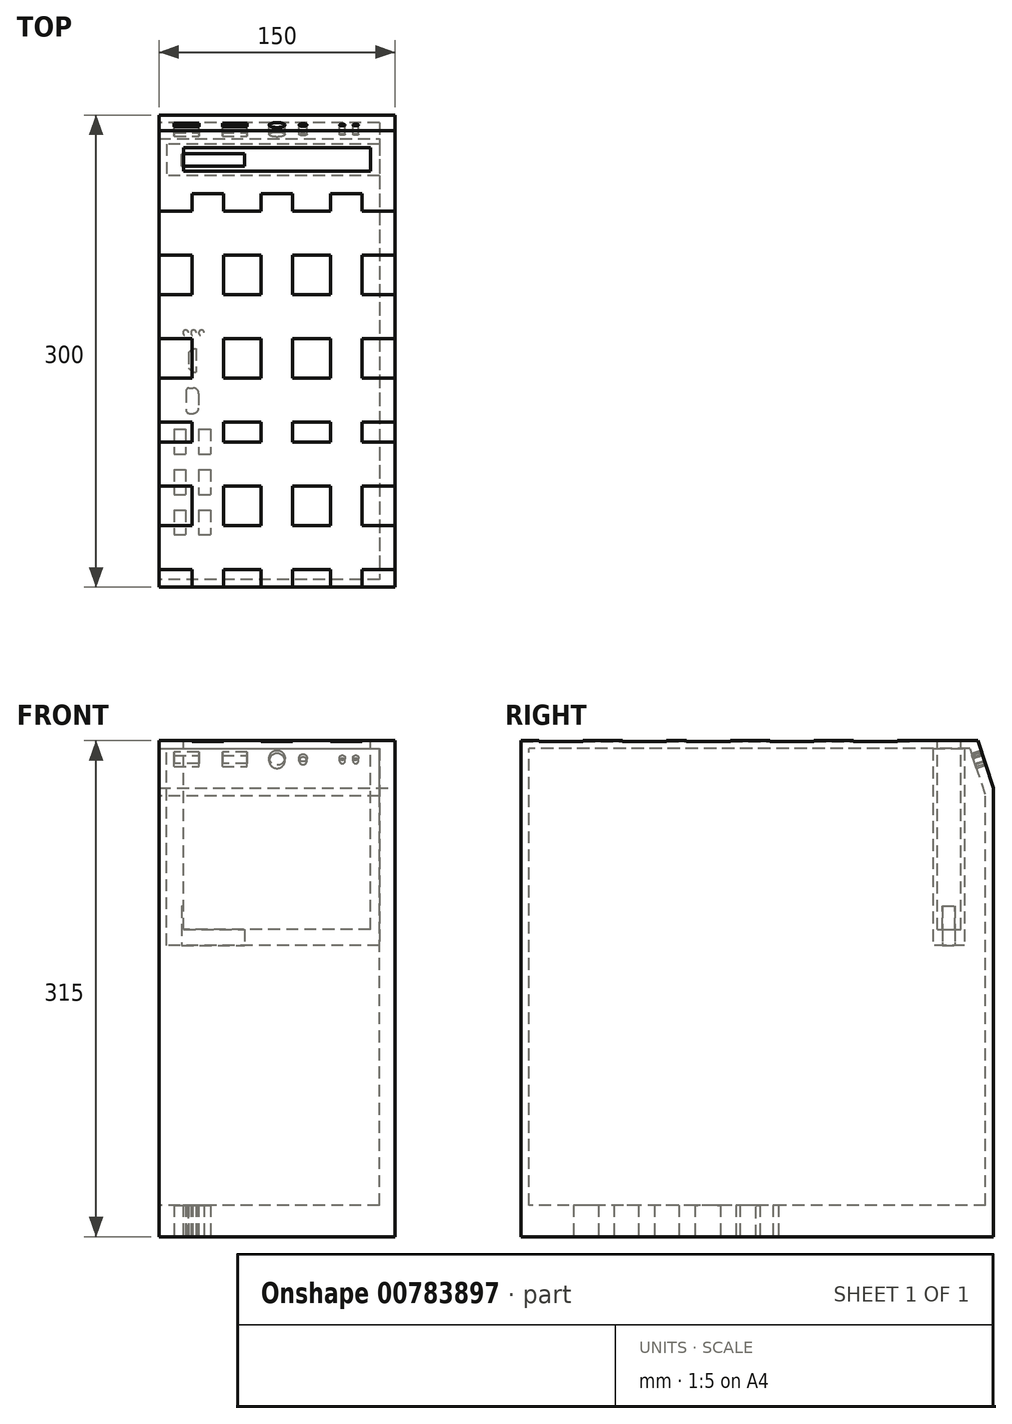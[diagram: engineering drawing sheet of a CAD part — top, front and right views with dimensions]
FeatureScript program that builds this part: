
annotation { "Feature Type Name" : "Feature", "Feature Type Description" : "" }
export const myFeature = defineFeature(function(context is Context, id is Id, definition is map)
    precondition{}
    {
        {
            var Q0;
            Q0=qCreatedBy(makeId("Top.planeOp"),FACE);
            var sketch = newSketch(context, id + "F0", { "sketchPlane" : qUnion([Q0])});
            skLineSegment(sketch, "E0.bottom", {"start": v(75, -150) * mm, "end": v(-75, -150) * mm});
            skLineSegment(sketch, "E0.top", {"start": v(75, 150) * mm, "end": v(-75, 150) * mm});
            skLineSegment(sketch, "E0.left", {"start": v(75, -150) * mm, "end": v(75, 150) * mm});
            skLineSegment(sketch, "E0.right", {"start": v(-75, -150) * mm, "end": v(-75, 150) * mm});
            skPoint(sketch, "E0.middle", {"position": v(0, 0) * mm});
            skSolve(sketch);
        }
        {
            var Q0;
            Q0=qSketchRegion(id+"F0",true);
            extrude(context, id + "F1", {"entities" : qUnion([Q0]), "depth" : 300 * mm, "offsetDistance" : 25 * mm});
        }
        {
            var Q0;
            Q0=makeQuery(id+"F1.opExtrude","SWEPT_FACE",FACE,{"disambiguationData":[OSD([sQuery(id+"F0.wireOp",EDGE,"E0.left")])]});
            var sketch = newSketch(context, id + "F2", { "sketchPlane" : qUnion([Q0])});
            skLineSegment(sketch, "E1.bottom", {"start": v(145, 295) * mm, "end": v(-145, 295) * mm});
            skLineSegment(sketch, "E1.top", {"start": v(145, 5) * mm, "end": v(-145, 5) * mm});
            skLineSegment(sketch, "E1.left", {"start": v(145, 295) * mm, "end": v(145, 5) * mm});
            skLineSegment(sketch, "E1.right", {"start": v(-145, 295) * mm, "end": v(-145, 5) * mm});
            skPoint(sketch, "E1.middle", {"position": v(0, 150) * mm});
            skPoint(sketch, "E1.middle.positionSnap0", {"position": v(-150, 150) * mm});
            skPoint(sketch, "E1.centerSnap0", {"position": v(-150, 150) * mm});
            skSolve(sketch);
        }
        {
            var Q0;
            Q0=qSketchRegion(id+"F2",true);
            extrude(context, id + "F3", {"entities" : qUnion([Q0]), "operationType" : NewBodyOperationType.REMOVE, "oppositeDirection" : true, "depth" : 140 * mm, "offsetDistance" : 25 * mm});
        }
        {
            var Q0;
            Q0=qCreatedBy(makeId("Top.planeOp"),FACE);
            var sketch = newSketch(context, id + "F4", { "sketchPlane" : qUnion([Q0])});
            skLineSegment(sketch, "E2.bottom", {"start": v(-70, 131.53) * mm, "end": v(70, 131.53) * mm});
            skLineSegment(sketch, "E2.top", {"start": v(-70, 111.53) * mm, "end": v(70, 111.53) * mm});
            skLineSegment(sketch, "E2.left", {"start": v(-70, 131.53) * mm, "end": v(-70, 111.53) * mm});
            skLineSegment(sketch, "E2.right", {"start": v(70, 131.53) * mm, "end": v(70, 111.53) * mm});
            skPoint(sketch, "E2.middle", {"position": v(0, 121.53) * mm});
            skSolve(sketch);
        }
        {
            var Q0;
            Q0=qSketchRegion(id+"F4",true);
            extrude(context, id + "F5", {"entities" : qUnion([Q0]), "operationType" : NewBodyOperationType.ADD, "depth" : 130 * mm, "offsetDistance" : 25 * mm});
        }
        {
            var Q0;
            Q0=makeQuery(id+"F4.imprint","IMPRINT",FACE,{"disambiguationData":[TD([[makeQuery(id+"F4.imprint","IMPRINT",EDGE,{"derivedFrom":sQuery(id+"F4.wireOp",EDGE,"E2.bottom")}),-1.0]])]});
            var sketch = newSketch(context, id + "F6", { "sketchPlane" : qUnion([Q0])});
            skLineSegment(sketch, "E3.bottom", {"start": v(-59.38, 114.4) * mm, "end": v(59.38, 114.4) * mm});
            skLineSegment(sketch, "E3.top", {"start": v(-59.38, 129.2) * mm, "end": v(59.38, 129.2) * mm});
            skLineSegment(sketch, "E3.left", {"start": v(-59.38, 114.4) * mm, "end": v(-59.38, 129.2) * mm});
            skLineSegment(sketch, "E3.right", {"start": v(59.38, 114.4) * mm, "end": v(59.38, 129.2) * mm});
            skPoint(sketch, "E3.middle", {"position": v(0, 121.8) * mm});
            skSolve(sketch);
        }
        {
            var Q0;
            Q0=qSketchRegion(id+"F6",true);
            extrude(context, id + "F7", {"entities" : qUnion([Q0]), "operationType" : NewBodyOperationType.REMOVE, "oppositeDirection" : true, "depth" : -120 * mm, "offsetDistance" : 25 * mm});
        }
        {
            var Q0;
            Q0=makeQuery(id+"F1.opExtrude","SWEPT_BODY",BODY,{"disambiguationData":[OSD([sQuery(id+"F0.wireOp",EDGE,"E0.bottom"),sQuery(id+"F0.wireOp",EDGE,"E0.top"),sQuery(id+"F0.wireOp",EDGE,"E0.left"),sQuery(id+"F0.wireOp",EDGE,"E0.right")])]});
            var Q1;
            Q1=sQuery(id+"F2.wireOp",EDGE,"E1.right");
            transform(context, id + "F8", {"entities" : qUnion([Q0]), "transformType" : TransformType.ROTATION, "transformAxis" : qUnion([Q1]), "angle" : 180 * degree, "makeCopy" : false});
        }
        {
            var Q0;
            Q0=makeQuery(id+"F1.opExtrude","SWEPT_BODY",BODY,{"disambiguationData":[OSD([sQuery(id+"F0.wireOp",EDGE,"E0.bottom"),sQuery(id+"F0.wireOp",EDGE,"E0.top"),sQuery(id+"F0.wireOp",EDGE,"E0.left"),sQuery(id+"F0.wireOp",EDGE,"E0.right")])]});
            var Q1;
            Q1=makeQuery(id+"F1.opExtrude","CAP_EDGE",EDGE,{"disambiguationData":[OSD([sQuery(id+"F0.wireOp",EDGE,"E0.bottom")])],"isStart":true});
            transform(context, id + "F9", {"entities" : qUnion([Q0]), "transformType" : TransformType.ROTATION, "transformAxis" : qUnion([Q1]), "angle" : 180 * degree, "makeCopy" : false});
        }
        {
            var Q0;
            Q0=makeQuery(id+"F1.opExtrude","CAP_EDGE",EDGE,{"disambiguationData":[OSD([sQuery(id+"F0.wireOp",EDGE,"E0.top")])],"isStart":true});
            var Q1;
            Q1=makeQuery(id+"F3.boolean.opBoolean","COPY",EDGE,{"derivedFrom":makeQuery(id+"F3.opExtrude","SWEPT_EDGE",EDGE,{"disambiguationData":[OSD([sQuery(id+"F2.wireOp",EDGE,"E1.top"),sQuery(id+"F2.wireOp",EDGE,"E1.left")])]})});
            chamfer(context, id + "F10", {"entities" : qUnion([Q0, Q1]), "chamferType" : ChamferType.TWO_OFFSETS, "width1" : 30 * mm, "oppositeDirection" : false, "width2" : 10 * mm, "tangentPropagation" : true});
        }
        {
            var Q0;
            Q0=makeQuery(id+"F10.opChamfer","BLEND_FACE",FACE,{"disambiguationData":[OSD([sQuery(id+"F0.wireOp",EDGE,"E0.top")])]});
            var sketch = newSketch(context, id + "F11", { "sketchPlane" : qUnion([Q0])});
            skLineSegment(sketch, "E4.bottom", {"start": v(-100.37, -55.09) * mm, "end": v(-84.67, -55.09) * mm});
            skLineSegment(sketch, "E4.top", {"start": v(-100.37, -62.59) * mm, "end": v(-84.67, -62.59) * mm});
            skLineSegment(sketch, "E4.left", {"start": v(-100.37, -55.09) * mm, "end": v(-100.37, -62.59) * mm});
            skLineSegment(sketch, "E4.right", {"start": v(-84.67, -55.09) * mm, "end": v(-84.67, -62.59) * mm});
            skPoint(sketch, "E4.middle", {"position": v(-92.52, -58.84) * mm});
            skLineSegment(sketch, "E5.bottom", {"start": v(-131.07, -55.09) * mm, "end": v(-115.37, -55.09) * mm});
            skLineSegment(sketch, "E5.top", {"start": v(-131.07, -62.59) * mm, "end": v(-115.37, -62.59) * mm});
            skLineSegment(sketch, "E5.left", {"start": v(-131.07, -55.09) * mm, "end": v(-131.07, -62.59) * mm});
            skLineSegment(sketch, "E5.right", {"start": v(-115.37, -55.09) * mm, "end": v(-115.37, -62.59) * mm});
            skPoint(sketch, "E5.middle", {"position": v(-123.22, -58.84) * mm});
            skPoint(sketch, "E5.cornerSnap0", {"position": v(-92.52, -55.09) * mm});
            skCircle(sketch, "E6", {"center": v(-191.47, -58.84) * mm, "radius": 1.75 * mm});
            skCircle(sketch, "E7", {"center": v(-199.97, -58.84) * mm, "radius": 1.75 * mm});
            skCircle(sketch, "E8", {"center": v(-150, -58.84) * mm, "radius": 5 * mm});
            skPoint(sketch, "E8.centerSnap0", {"position": v(-131.07, -58.84) * mm});
            skCircle(sketch, "E9", {"center": v(-166.5, -58.84) * mm, "radius": 2.5 * mm});
            skSolve(sketch);
        }
        {
            var Q0;
            Q0=qSketchRegion(id+"F11",true);
            extrude(context, id + "F12", {"entities" : qUnion([Q0]), "operationType" : NewBodyOperationType.REMOVE, "oppositeDirection" : true, "depth" : 10 * mm, "offsetDistance" : 25 * mm});
        }
        {
            var Q0;
            Q0=makeQuery(id+"F11.imprint","IMPRINT",FACE,{"disambiguationData":[TD([[makeQuery(id+"F11.imprint","IMPRINT",EDGE,{"derivedFrom":sQuery(id+"F11.wireOp",EDGE,"E5.bottom")}),-1.0]])]});
            extrude(context, id + "F13", {"entities" : qUnion([Q0]), "operationType" : NewBodyOperationType.REMOVE, "oppositeDirection" : true, "depth" : 10 * mm, "offsetDistance" : 25 * mm});
        }
        {
            var Q0;
            Q0=makeQuery(id+"F1.opExtrude","CAP_FACE",FACE,{"disambiguationData":[OSD([sQuery(id+"F0.wireOp",EDGE,"E0.bottom"),sQuery(id+"F0.wireOp",EDGE,"E0.top"),sQuery(id+"F0.wireOp",EDGE,"E0.left"),sQuery(id+"F0.wireOp",EDGE,"E0.right")])],"isStart":false});
            var sketch = newSketch(context, id + "F14", { "sketchPlane" : qUnion([Q0])});
            skLineSegment(sketch, "E10.bottom", {"start": v(100.26, 91) * mm, "end": v(107.76, 91) * mm});
            skLineSegment(sketch, "E10.top", {"start": v(100.26, 106.7) * mm, "end": v(107.76, 106.7) * mm});
            skLineSegment(sketch, "E10.left", {"start": v(100.26, 91) * mm, "end": v(100.26, 106.7) * mm});
            skLineSegment(sketch, "E10.right", {"start": v(107.76, 91) * mm, "end": v(107.76, 106.7) * mm});
            skPoint(sketch, "E10.middle", {"position": v(104, 98.84) * mm});
            skLineSegment(sketch, "E11.bottom", {"start": v(84.56, 91) * mm, "end": v(92.06, 91) * mm});
            skLineSegment(sketch, "E11.top", {"start": v(84.56, 106.7) * mm, "end": v(92.06, 106.7) * mm});
            skLineSegment(sketch, "E11.left", {"start": v(84.56, 91) * mm, "end": v(84.56, 106.7) * mm});
            skLineSegment(sketch, "E11.right", {"start": v(92.06, 91) * mm, "end": v(92.06, 106.7) * mm});
            skPoint(sketch, "E11.middle", {"position": v(88.3, 98.84) * mm});
            skLineSegment(sketch, "E12.bottom", {"start": v(100.26, 65.3) * mm, "end": v(107.76, 65.3) * mm});
            skLineSegment(sketch, "E12.top", {"start": v(100.26, 81) * mm, "end": v(107.76, 81) * mm});
            skLineSegment(sketch, "E12.left", {"start": v(100.26, 65.3) * mm, "end": v(100.26, 81) * mm});
            skLineSegment(sketch, "E12.right", {"start": v(107.76, 65.3) * mm, "end": v(107.76, 81) * mm});
            skPoint(sketch, "E12.middle", {"position": v(104, 73.14) * mm});
            skLineSegment(sketch, "E13.bottom", {"start": v(84.56, 65.3) * mm, "end": v(92.06, 65.3) * mm});
            skLineSegment(sketch, "E13.top", {"start": v(84.56, 81) * mm, "end": v(92.06, 81) * mm});
            skLineSegment(sketch, "E13.left", {"start": v(84.56, 65.3) * mm, "end": v(84.56, 81) * mm});
            skLineSegment(sketch, "E13.right", {"start": v(92.06, 65.3) * mm, "end": v(92.06, 81) * mm});
            skPoint(sketch, "E13.middle", {"position": v(88.3, 73.14) * mm});
            skPoint(sketch, "E13.middle.positionSnap0", {"position": v(88.3, 91) * mm});
            skPoint(sketch, "E13.centerSnap0", {"position": v(88.3, 91) * mm});
            skLineSegment(sketch, "E14.bottom", {"start": v(100.26, 39.6) * mm, "end": v(107.76, 39.6) * mm});
            skLineSegment(sketch, "E14.top", {"start": v(100.26, 55.3) * mm, "end": v(107.76, 55.3) * mm});
            skLineSegment(sketch, "E14.left", {"start": v(100.26, 39.6) * mm, "end": v(100.26, 55.3) * mm});
            skLineSegment(sketch, "E14.right", {"start": v(107.76, 39.6) * mm, "end": v(107.76, 55.3) * mm});
            skPoint(sketch, "E14.middle", {"position": v(104, 47.44) * mm});
            skLineSegment(sketch, "E15.bottom", {"start": v(84.56, 39.6) * mm, "end": v(92.06, 39.6) * mm});
            skLineSegment(sketch, "E15.top", {"start": v(84.56, 55.3) * mm, "end": v(92.06, 55.3) * mm});
            skLineSegment(sketch, "E15.left", {"start": v(84.56, 39.6) * mm, "end": v(84.56, 55.3) * mm});
            skLineSegment(sketch, "E15.right", {"start": v(92.06, 39.6) * mm, "end": v(92.06, 55.3) * mm});
            skPoint(sketch, "E15.middle", {"position": v(88.3, 47.44) * mm});
            skSolve(sketch);
        }
        {
            var Q0;
            Q0=qSketchRegion(id+"F14",true);
            extrude(context, id + "F15", {"entities" : qUnion([Q0]), "operationType" : NewBodyOperationType.REMOVE, "oppositeDirection" : true, "depth" : 10 * mm, "offsetDistance" : 25 * mm});
        }
        {
            var Q0;
            Q0=makeQuery(id+"F1.opExtrude","CAP_FACE",FACE,{"disambiguationData":[OSD([sQuery(id+"F0.wireOp",EDGE,"E0.bottom"),sQuery(id+"F0.wireOp",EDGE,"E0.top"),sQuery(id+"F0.wireOp",EDGE,"E0.left"),sQuery(id+"F0.wireOp",EDGE,"E0.right")])],"isStart":false});
            extrude(context, id + "F16", {"entities" : qUnion([Q0]), "operationType" : NewBodyOperationType.ADD, "depth" : 25 * mm, "offsetDistance" : 25 * mm});
        }
        {
            var Q0;
            Q0=makeQuery(id+"F16.opExtrude","CAP_FACE",FACE,{"disambiguationData":[OSD([sQuery(id+"F0.wireOp",EDGE,"E0.bottom"),sQuery(id+"F0.wireOp",EDGE,"E0.top"),sQuery(id+"F0.wireOp",EDGE,"E0.left"),sQuery(id+"F0.wireOp",EDGE,"E0.right")])],"isStart":false});
            var sketch = newSketch(context, id + "F17", { "sketchPlane" : qUnion([Q0])});
            skLineSegment(sketch, "E16.bottom", {"start": v(92.28, 13.4) * mm, "end": v(100.18, 13.4) * mm});
            skLineSegment(sketch, "E16.top", {"start": v(92.28, 29.6) * mm, "end": v(100.18, 29.6) * mm});
            skLineSegment(sketch, "E16.left", {"start": v(92.28, 13.4) * mm, "end": v(92.28, 29.6) * mm});
            skLineSegment(sketch, "E16.right", {"start": v(100.18, 13.4) * mm, "end": v(100.18, 29.6) * mm});
            skPoint(sketch, "E16.middle", {"position": v(96.23, 21.5) * mm});
            skLineSegment(sketch, "E17.bottom", {"start": v(93.73, -11.6) * mm, "end": v(98.73, -11.6) * mm});
            skLineSegment(sketch, "E17.top", {"start": v(93.73, 3.4) * mm, "end": v(98.73, 3.4) * mm});
            skLineSegment(sketch, "E17.left", {"start": v(93.73, -11.6) * mm, "end": v(93.73, 3.4) * mm});
            skLineSegment(sketch, "E17.right", {"start": v(98.73, -11.6) * mm, "end": v(98.73, 3.4) * mm});
            skPoint(sketch, "E17.middle", {"position": v(96.23, -4.1) * mm});
            skPoint(sketch, "E18.centerSnap0", {"position": v(104, 39.6) * mm});
            skCircle(sketch, "E19", {"center": v(102, -21.6) * mm, "radius": 1.75 * mm});
            skCircle(sketch, "E20", {"center": v(97, -21.6) * mm, "radius": 1.75 * mm});
            skCircle(sketch, "E21", {"center": v(92, -21.6) * mm, "radius": 1.75 * mm});
            skSolve(sketch);
        }
        {
            var Q0;
            Q0=makeQuery(id+"F17.imprint","IMPRINT",FACE,{"disambiguationData":[TD([[makeQuery(id+"F17.imprint","IMPRINT",EDGE,{"derivedFrom":sQuery(id+"F17.wireOp",EDGE,"E16.bottom")}),-1.0]])]});
            extrude(context, id + "F18", {"entities" : qUnion([Q0]), "operationType" : NewBodyOperationType.REMOVE, "oppositeDirection" : true, "depth" : 10 * mm, "offsetDistance" : 25 * mm});
        }
        {
            var Q0;
            Q0=qSketchRegion(id+"F17",true);
            extrude(context, id + "F19", {"entities" : qUnion([Q0]), "operationType" : NewBodyOperationType.REMOVE, "oppositeDirection" : true, "depth" : 50 * mm, "offsetDistance" : 25 * mm});
        }
        {
            var Q0;
            Q0=makeQuery(id+"F19.boolean.opBoolean","COPY",EDGE,{"derivedFrom":makeQuery(id+"F19.opExtrude","SWEPT_EDGE",EDGE,{"disambiguationData":[OSD([sQuery(id+"F17.wireOp",EDGE,"E16.bottom"),sQuery(id+"F17.wireOp",EDGE,"E16.right")])]})});
            var Q1;
            Q1=makeQuery(id+"F19.boolean.opBoolean","COPY",EDGE,{"derivedFrom":makeQuery(id+"F19.opExtrude","SWEPT_EDGE",EDGE,{"disambiguationData":[OSD([sQuery(id+"F17.wireOp",EDGE,"E16.top"),sQuery(id+"F17.wireOp",EDGE,"E16.right")])]})});
            fillet(context, id + "F20", {"entities" : qUnion([Q0, Q1]), "radius" : 3.5 * mm, "tangentPropagation" : true, "allowEdgeOverflow" : false});
        }
        {
            var Q0;
            Q0=makeQuery(id+"F19.boolean.opBoolean","COPY",EDGE,{"derivedFrom":makeQuery(id+"F19.opExtrude","SWEPT_EDGE",EDGE,{"disambiguationData":[OSD([sQuery(id+"F17.wireOp",EDGE,"E16.top"),sQuery(id+"F17.wireOp",EDGE,"E16.left")])]})});
            var Q1;
            Q1=makeQuery(id+"F19.boolean.opBoolean","COPY",EDGE,{"derivedFrom":makeQuery(id+"F19.opExtrude","SWEPT_EDGE",EDGE,{"disambiguationData":[OSD([sQuery(id+"F17.wireOp",EDGE,"E16.bottom"),sQuery(id+"F17.wireOp",EDGE,"E16.left")])]})});
            fillet(context, id + "F21", {"entities" : qUnion([Q0, Q1]), "radius" : 2 * mm, "tangentPropagation" : true, "allowEdgeOverflow" : false});
        }
        {
            var Q0;
            Q0=makeQuery(id+"F19.boolean.opBoolean","COPY",EDGE,{"derivedFrom":makeQuery(id+"F19.opExtrude","SWEPT_EDGE",EDGE,{"disambiguationData":[OSD([sQuery(id+"F17.wireOp",EDGE,"E17.bottom"),sQuery(id+"F17.wireOp",EDGE,"E17.left")])]})});
            var Q1;
            Q1=makeQuery(id+"F19.boolean.opBoolean","COPY",EDGE,{"derivedFrom":makeQuery(id+"F19.opExtrude","SWEPT_EDGE",EDGE,{"disambiguationData":[OSD([sQuery(id+"F17.wireOp",EDGE,"E17.top"),sQuery(id+"F17.wireOp",EDGE,"E17.left")])]})});
            chamfer(context, id + "F22", {"entities" : qUnion([Q0, Q1]), "width" : 2.5 * mm, "tangentPropagation" : true});
        }
        {
            var Q0;
            Q0=makeQuery(id+"F5.opExtrude","CAP_FACE",FACE,{"disambiguationData":[OSD([sQuery(id+"F4.wireOp",EDGE,"E2.bottom"),sQuery(id+"F4.wireOp",EDGE,"E2.top"),sQuery(id+"F4.wireOp",EDGE,"E2.left"),sQuery(id+"F4.wireOp",EDGE,"E2.right")])],"isStart":false});
            var sketch = newSketch(context, id + "F23", { "sketchPlane" : qUnion([Q0])});
            skLineSegment(sketch, "E22.bottom", {"start": v(89.4, -127.53) * mm, "end": v(129.4, -127.53) * mm});
            skLineSegment(sketch, "E22.top", {"start": v(89.4, -135.53) * mm, "end": v(129.4, -135.53) * mm});
            skLineSegment(sketch, "E22.left", {"start": v(89.4, -127.53) * mm, "end": v(89.4, -135.53) * mm});
            skLineSegment(sketch, "E22.right", {"start": v(129.4, -127.53) * mm, "end": v(129.4, -135.53) * mm});
            skPoint(sketch, "E22.middle", {"position": v(109.4, -131.53) * mm});
            skSolve(sketch);
        }
        {
            var Q0;
            Q0=qSketchRegion(id+"F23",true);
            extrude(context, id + "F24", {"entities" : qUnion([Q0]), "operationType" : NewBodyOperationType.REMOVE, "oppositeDirection" : true, "depth" : 25 * mm, "offsetDistance" : 25 * mm});
        }
        {
            var Q0;
            Q0=makeQuery(id+"F1.opExtrude","CAP_FACE",FACE,{"disambiguationData":[OSD([sQuery(id+"F0.wireOp",EDGE,"E0.bottom"),sQuery(id+"F0.wireOp",EDGE,"E0.top"),sQuery(id+"F0.wireOp",EDGE,"E0.left"),sQuery(id+"F0.wireOp",EDGE,"E0.right")])],"isStart":true});
            var sketch = newSketch(context, id + "F25", { "sketchPlane" : qUnion([Q0])});
            skLineSegment(sketch, "E23.bottom", {"start": v(96, -140) * mm, "end": v(116, -140) * mm});
            skLineSegment(sketch, "E23.top", {"start": v(96, 110) * mm, "end": v(116, 110) * mm});
            skLineSegment(sketch, "E23.left", {"start": v(96, -140) * mm, "end": v(96, 110) * mm});
            skLineSegment(sketch, "E23.right", {"start": v(116, -140) * mm, "end": v(116, 110) * mm});
            skPoint(sketch, "E23.middle", {"position": v(106, -15) * mm});
            skLineSegment(sketch, "E24.bottom", {"start": v(160, -140) * mm, "end": v(140, -140) * mm});
            skLineSegment(sketch, "E24.top", {"start": v(160, 110) * mm, "end": v(140, 110) * mm});
            skLineSegment(sketch, "E24.left", {"start": v(160, -140) * mm, "end": v(160, 110) * mm});
            skLineSegment(sketch, "E24.right", {"start": v(140, -140) * mm, "end": v(140, 110) * mm});
            skPoint(sketch, "E24.middle", {"position": v(150, -15) * mm});
            skPoint(sketch, "E24.middle.positionSnap0", {"position": v(116, -15) * mm});
            skPoint(sketch, "E24.centerSnap0", {"position": v(116, -15) * mm});
            skLineSegment(sketch, "E25.bottom", {"start": v(204, -140) * mm, "end": v(184, -140) * mm});
            skLineSegment(sketch, "E25.top", {"start": v(204, 110) * mm, "end": v(184, 110) * mm});
            skLineSegment(sketch, "E25.left", {"start": v(204, -140) * mm, "end": v(204, 110) * mm});
            skLineSegment(sketch, "E25.right", {"start": v(184, -140) * mm, "end": v(184, 110) * mm});
            skPoint(sketch, "E25.middle", {"position": v(194, -15) * mm});
            skSolve(sketch);
        }
        {
            var Q0;
            Q0=qSketchRegion(id+"F25",true);
            extrude(context, id + "F26", {"entities" : qUnion([Q0]), "operationType" : NewBodyOperationType.REMOVE, "oppositeDirection" : true, "depth" : 0.5 * mm, "offsetDistance" : 25 * mm});
        }
        {
            var Q0;
            Q0=makeQuery(id+"F1.opExtrude","CAP_FACE",FACE,{"disambiguationData":[OSD([sQuery(id+"F0.wireOp",EDGE,"E0.bottom"),sQuery(id+"F0.wireOp",EDGE,"E0.top"),sQuery(id+"F0.wireOp",EDGE,"E0.left"),sQuery(id+"F0.wireOp",EDGE,"E0.right")])],"isStart":true});
            var sketch = newSketch(context, id + "F27", { "sketchPlane" : qUnion([Q0])});
            skPoint(sketch, "E26.middle.positionSnap0", {"position": v(106, 110) * mm});
            skPoint(sketch, "E26.centerSnap0", {"position": v(106, 110) * mm});
            skLineSegment(sketch, "E27.bottom", {"start": v(225, 99.01) * mm, "end": v(75, 99.01) * mm});
            skLineSegment(sketch, "E27.top", {"start": v(225, 70.99) * mm, "end": v(75, 70.99) * mm});
            skLineSegment(sketch, "E27.left", {"start": v(225, 99.01) * mm, "end": v(225, 70.99) * mm});
            skLineSegment(sketch, "E27.right", {"start": v(75, 99.01) * mm, "end": v(75, 70.99) * mm});
            skPoint(sketch, "E27.middle", {"position": v(150, 85) * mm});
            skLineSegment(sketch, "E28.bottom", {"start": v(225, 45.99) * mm, "end": v(75, 45.99) * mm});
            skLineSegment(sketch, "E28.top", {"start": v(225, 17.96) * mm, "end": v(75, 17.96) * mm});
            skLineSegment(sketch, "E28.left", {"start": v(225, 45.99) * mm, "end": v(225, 17.96) * mm});
            skLineSegment(sketch, "E28.right", {"start": v(75, 45.99) * mm, "end": v(75, 17.96) * mm});
            skPoint(sketch, "E28.middle", {"position": v(150, 31.97) * mm});
            skLineSegment(sketch, "E29.bottom", {"start": v(225, -7.04) * mm, "end": v(75, -7.04) * mm});
            skLineSegment(sketch, "E29.top", {"start": v(225, -35.07) * mm, "end": v(75, -35.07) * mm});
            skLineSegment(sketch, "E29.left", {"start": v(225, -7.04) * mm, "end": v(225, -35.07) * mm});
            skLineSegment(sketch, "E29.right", {"start": v(75, -7.04) * mm, "end": v(75, -35.07) * mm});
            skPoint(sketch, "E29.middle", {"position": v(150, -21.06) * mm});
            skLineSegment(sketch, "E30.bottom", {"start": v(225, -75.68) * mm, "end": v(75, -75.68) * mm});
            skLineSegment(sketch, "E30.top", {"start": v(225, -47.65) * mm, "end": v(75, -47.65) * mm});
            skLineSegment(sketch, "E30.left", {"start": v(225, -75.68) * mm, "end": v(225, -47.65) * mm});
            skLineSegment(sketch, "E30.right", {"start": v(75, -75.68) * mm, "end": v(75, -47.65) * mm});
            skPoint(sketch, "E30.middle", {"position": v(150, -61.66) * mm});
            skLineSegment(sketch, "E31.bottom", {"start": v(225, -128.7) * mm, "end": v(75, -128.7) * mm});
            skLineSegment(sketch, "E31.top", {"start": v(225, -100.68) * mm, "end": v(75, -100.68) * mm});
            skLineSegment(sketch, "E31.left", {"start": v(225, -128.7) * mm, "end": v(225, -100.68) * mm});
            skLineSegment(sketch, "E31.right", {"start": v(75, -128.7) * mm, "end": v(75, -100.68) * mm});
            skPoint(sketch, "E31.middle", {"position": v(150, -114.7) * mm});
            skSolve(sketch);
        }
        {
            var Q0;
            Q0=qSketchRegion(id+"F27",true);
            extrude(context, id + "F28", {"entities" : qUnion([Q0]), "operationType" : NewBodyOperationType.REMOVE, "oppositeDirection" : true, "depth" : 0.5 * mm, "offsetDistance" : 25 * mm});
        }
    });
